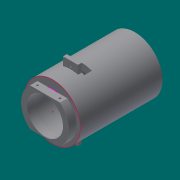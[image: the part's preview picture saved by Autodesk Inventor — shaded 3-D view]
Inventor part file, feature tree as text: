
AUTODESK INVENTOR PART (.ipt)
format: ipt  version: 2013 (Build 170138000, 138)  size: 214,528 bytes
history: native  units: mm
features: sketch x8, extrude x6, other x3, revolve x1, mirror x1
ambient origin geometry x8: Origin, YZ Plane, XZ Plane, XY Plane, X Axis, Y Axis, Z Axis, Center Point
feature tree (19):
  other  "ソリッド1"
  revolve  "回転1"
  other  "作業平面4"
  sketch  "スケッチ2"
  sketch  "スケッチ3"
  extrude  "押し出し1"  Depth=32.0mm
  extrude  "押し出し2"  Depth=30.0mm
  extrude  "押し出し3"  Depth=35.0mm
  extrude  "押し出し4"  Depth=2.0mm
  extrude  "押し出し5"  Depth=80.0mm
  mirror  "ミラー1"
  other  "作業平面5"
  extrude  "押し出し7"  TaperAngle=90.0deg  [1 undecoded]
  sketch  "スケッチ1"
  sketch  "スケッチ4"
  sketch  "スケッチ5"
  sketch  "スケッチ6"
  sketch  "スケッチ7"
  sketch  "スケッチ8"
note: 1 required parameter value undecoded (feature->parameter linkage not recoverable at this tier; creation-order binding heuristic only, values carry confidence <= 0.55)
